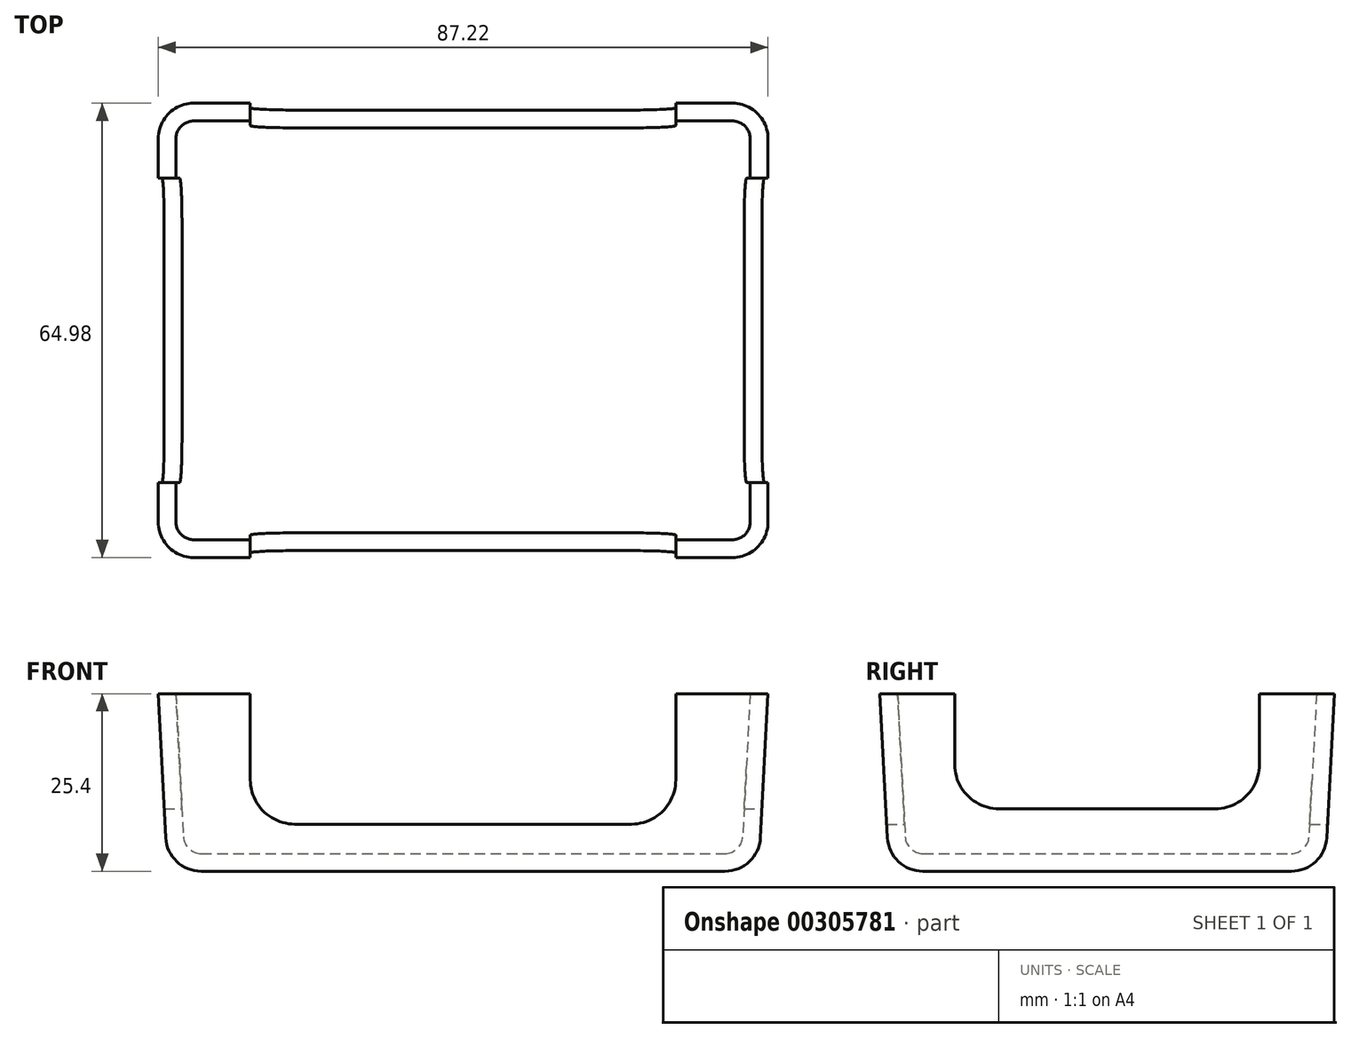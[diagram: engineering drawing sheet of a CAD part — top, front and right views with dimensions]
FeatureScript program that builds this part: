
annotation { "Feature Type Name" : "Feature", "Feature Type Description" : "" }
export const myFeature = defineFeature(function(context is Context, id is Id, definition is map)
    precondition{}
    {
        {
            var Q0;
            Q0=qCreatedBy(makeId("Top.planeOp"),FACE);
            var sketch = newSketch(context, id + "F0", { "sketchPlane" : qUnion([Q0])});
            skLineSegment(sketch, "E0.bottom", {"start": v(42.27, 31.16) * mm, "end": v(-42.27, 31.16) * mm});
            skLineSegment(sketch, "E0.top", {"start": v(42.27, -31.16) * mm, "end": v(-42.27, -31.16) * mm});
            skLineSegment(sketch, "E0.left", {"start": v(42.27, 31.16) * mm, "end": v(42.27, -31.16) * mm});
            skLineSegment(sketch, "E0.right", {"start": v(-42.27, 31.16) * mm, "end": v(-42.27, -31.16) * mm});
            skPoint(sketch, "E0.middle", {"position": v(0, 0) * mm});
            skSolve(sketch);
        }
        {
            var Q0;
            Q0=makeQuery(id+"F0.imprint","IMPRINT",FACE,{"disambiguationData":[TD([[makeQuery(id+"F0.imprint","IMPRINT",EDGE,{"derivedFrom":sQuery(id+"F0.wireOp",EDGE,"E0.bottom")}),1.0]])]});
            extrude(context, id + "F1", {"entities" : qUnion([Q0]), "depth" : 25.4 * mm, "hasDraft" : true, "draftAngle" : 3 * degree});
        }
        {
            var Q0;
            Q0=makeQuery(id+"F1.opExtrude","SWEPT_EDGE",EDGE,{"disambiguationData":[OSD([sQuery(id+"F0.wireOp",EDGE,"E0.top"),sQuery(id+"F0.wireOp",EDGE,"E0.right")])]});
            var Q1;
            Q1=makeQuery(id+"F1.opExtrude","SWEPT_EDGE",EDGE,{"disambiguationData":[OSD([sQuery(id+"F0.wireOp",EDGE,"E0.top"),sQuery(id+"F0.wireOp",EDGE,"E0.left")])]});
            var Q2;
            Q2=makeQuery(id+"F1.opExtrude","CAP_EDGE",EDGE,{"disambiguationData":[OSD([sQuery(id+"F0.wireOp",EDGE,"E0.top")])],"isStart":true});
            var Q3;
            Q3=makeQuery(id+"F1.opExtrude","CAP_EDGE",EDGE,{"disambiguationData":[OSD([sQuery(id+"F0.wireOp",EDGE,"E0.right")])],"isStart":true});
            var Q4;
            Q4=makeQuery(id+"F1.opExtrude","SWEPT_EDGE",EDGE,{"disambiguationData":[OSD([sQuery(id+"F0.wireOp",EDGE,"E0.bottom"),sQuery(id+"F0.wireOp",EDGE,"E0.right")])]});
            var Q5;
            Q5=makeQuery(id+"F1.opExtrude","CAP_EDGE",EDGE,{"disambiguationData":[OSD([sQuery(id+"F0.wireOp",EDGE,"E0.bottom")])],"isStart":true});
            var Q6;
            Q6=makeQuery(id+"F1.opExtrude","CAP_EDGE",EDGE,{"disambiguationData":[OSD([sQuery(id+"F0.wireOp",EDGE,"E0.left")])],"isStart":true});
            var Q7;
            Q7=makeQuery(id+"F1.opExtrude","SWEPT_EDGE",EDGE,{"disambiguationData":[OSD([sQuery(id+"F0.wireOp",EDGE,"E0.bottom"),sQuery(id+"F0.wireOp",EDGE,"E0.left")])]});
            fillet(context, id + "F2", {"entities" : qUnion([Q0, Q1, Q2, Q3, Q4, Q5, Q6, Q7]), "radius" : 5.08 * mm, "tangentPropagation" : true, "allowEdgeOverflow" : false});
        }
        {
            var Q0;
            Q0=qCreatedBy(makeId("Front.planeOp"),FACE);
            var sketch = newSketch(context, id + "F3", { "sketchPlane" : qUnion([Q0])});
            skLineSegment(sketch, "E1.bottom", {"start": v(30.43, 44.07) * mm, "end": v(-30.43, 44.07) * mm});
            skLineSegment(sketch, "E1.top", {"start": v(24.08, 6.73) * mm, "end": v(-24.08, 6.73) * mm});
            skLineSegment(sketch, "E1.left", {"start": v(30.43, 44.07) * mm, "end": v(30.43, 13.08) * mm});
            skLineSegment(sketch, "E1.right", {"start": v(-30.43, 44.07) * mm, "end": v(-30.43, 13.08) * mm});
            skPoint(sketch, "E1.middle", {"position": v(0, 25.4) * mm});
            skPoint(sketch, "E2.visualSharp", {"position": v(-30.43, 6.73) * mm});
            skArc(sketch, "E2.filletArc", {"start": v(-30.43, 13.08) * mm, "mid": v(-28.57, 8.6) * mm, "end": v(-24.08, 6.73) * mm});
            skPoint(sketch, "E3.visualSharp", {"position": v(30.43, 6.73) * mm});
            skArc(sketch, "E3.filletArc", {"start": v(24.08, 6.73) * mm, "mid": v(28.57, 8.6) * mm, "end": v(30.43, 13.08) * mm});
            skSolve(sketch);
        }
        {
            var Q0;
            Q0=makeQuery(id+"F3.imprint","IMPRINT",FACE,{"disambiguationData":[TD([[makeQuery(id+"F3.imprint","IMPRINT",EDGE,{"derivedFrom":sQuery(id+"F3.wireOp",EDGE,"E1.bottom")}),1.0]])]});
            extrude(context, id + "F4", {"entities" : qUnion([Q0]), "operationType" : NewBodyOperationType.REMOVE, "depth" : 81.28 * mm, "symmetric" : true});
        }
        {
            var Q0;
            Q0=qCreatedBy(makeId("Right.planeOp"),FACE);
            var sketch = newSketch(context, id + "F5", { "sketchPlane" : qUnion([Q0])});
            skLineSegment(sketch, "E4.bottom", {"start": v(21.8, 38.98) * mm, "end": v(-21.8, 38.98) * mm});
            skLineSegment(sketch, "E4.top", {"start": v(15.45, 8.93) * mm, "end": v(-15.45, 8.93) * mm});
            skLineSegment(sketch, "E4.left", {"start": v(21.8, 38.98) * mm, "end": v(21.8, 15.28) * mm});
            skLineSegment(sketch, "E4.right", {"start": v(-21.8, 38.98) * mm, "end": v(-21.8, 15.28) * mm});
            skPoint(sketch, "E4.middle", {"position": v(0, 23.96) * mm});
            skPoint(sketch, "E5.visualSharp", {"position": v(-21.8, 8.93) * mm});
            skArc(sketch, "E5.filletArc", {"start": v(-21.8, 15.28) * mm, "mid": v(-19.94, 10.8) * mm, "end": v(-15.45, 8.93) * mm});
            skPoint(sketch, "E6.visualSharp", {"position": v(21.8, 8.93) * mm});
            skArc(sketch, "E6.filletArc", {"start": v(15.45, 8.93) * mm, "mid": v(19.94, 10.8) * mm, "end": v(21.8, 15.28) * mm});
            skSolve(sketch);
        }
        {
            var Q0;
            Q0=makeQuery(id+"F5.imprint","IMPRINT",FACE,{"disambiguationData":[TD([[makeQuery(id+"F5.imprint","IMPRINT",EDGE,{"derivedFrom":sQuery(id+"F5.wireOp",EDGE,"E4.bottom")}),1.0]])]});
            extrude(context, id + "F6", {"entities" : qUnion([Q0]), "operationType" : NewBodyOperationType.REMOVE, "oppositeDirection" : true, "depth" : 98.04 * mm, "hasSecondDirection" : true, "secondDirectionOppositeDirection" : false, "secondDirectionDepth" : 25.4 * mm, "symmetric" : true});
        }
        {
            var Q0;
            {var subQ0=sQuery(id+"F0.wireOp",EDGE,"E0.bottom");var subQ1=sQuery(id+"F0.wireOp",EDGE,"E0.right");var subQ2=sQuery(id+"F0.wireOp",EDGE,"E0.top");Q0=makeQuery(id+"F4.boolean.opBoolean","SPLIT",FACE,{"disambiguationData":[TD([makeQuery(id+"F1.opExtrude","SWEPT_FACE",FACE,{"disambiguationData":[OSD([subQ1])]})])],"derivedFrom":makeQuery(id+"F1.opExtrude","CAP_FACE",FACE,{"disambiguationData":[OSD([subQ0,subQ2,sQuery(id+"F0.wireOp",EDGE,"E0.left"),subQ1])],"isStart":false})});}
            var Q1;
            Q1=makeQuery(id+"F4.boolean.opBoolean","COPY",FACE,{"derivedFrom":makeQuery(id+"F4.opExtrude","SWEPT_FACE",FACE,{"disambiguationData":[OSD([sQuery(id+"F3.wireOp",EDGE,"E1.right")])]})});
            var Q2;
            Q2=makeQuery(id+"F4.boolean.opBoolean","COPY",FACE,{"derivedFrom":makeQuery(id+"F4.opExtrude","SWEPT_FACE",FACE,{"disambiguationData":[OSD([sQuery(id+"F3.wireOp",EDGE,"E1.top")])]})});
            var Q3;
            Q3=makeQuery(id+"F4.boolean.opBoolean","COPY",FACE,{"derivedFrom":makeQuery(id+"F4.opExtrude","SWEPT_FACE",FACE,{"disambiguationData":[OSD([sQuery(id+"F3.wireOp",EDGE,"E1.left")])]})});
            var Q4;
            {var subQ0=sQuery(id+"F0.wireOp",EDGE,"E0.bottom");var subQ1=sQuery(id+"F0.wireOp",EDGE,"E0.top");var subQ2=sQuery(id+"F0.wireOp",EDGE,"E0.left");Q4=makeQuery(id+"F4.boolean.opBoolean","SPLIT",FACE,{"disambiguationData":[TD([makeQuery(id+"F1.opExtrude","SWEPT_FACE",FACE,{"disambiguationData":[OSD([subQ2])]})])],"derivedFrom":makeQuery(id+"F1.opExtrude","CAP_FACE",FACE,{"disambiguationData":[OSD([subQ0,subQ1,subQ2,sQuery(id+"F0.wireOp",EDGE,"E0.right")])],"isStart":false})});}
            var Q5;
            Q5=makeQuery(id+"F4.boolean.opBoolean","COPY",FACE,{"derivedFrom":makeQuery(id+"F4.opExtrude","SWEPT_FACE",FACE,{"disambiguationData":[OSD([sQuery(id+"F3.wireOp",EDGE,"E3.filletArc")])]})});
            var Q6;
            Q6=makeQuery(id+"F4.boolean.opBoolean","COPY",FACE,{"derivedFrom":makeQuery(id+"F4.opExtrude","SWEPT_FACE",FACE,{"disambiguationData":[OSD([sQuery(id+"F3.wireOp",EDGE,"E2.filletArc")])]})});
            var Q7;
            {var subQ0=sQuery(id+"F0.wireOp",EDGE,"E0.right");Q7=makeQuery(id+"F6.boolean.opBoolean","COPY",FACE,{"disambiguationData":[TD([makeQuery(id+"F1.opExtrude","SWEPT_FACE",FACE,{"disambiguationData":[OSD([subQ0])]})])],"derivedFrom":makeQuery(id+"F6.opExtrude","SWEPT_FACE",FACE,{"disambiguationData":[OSD([sQuery(id+"F5.wireOp",EDGE,"E4.left")])]})});}
            var Q8;
            Q8=makeQuery(id+"F6.boolean.opBoolean","COPY",FACE,{"disambiguationData":[TD([makeQuery(id+"F1.opExtrude","SWEPT_FACE",FACE,{"disambiguationData":[OSD([sQuery(id+"F0.wireOp",EDGE,"E0.right")])]})])],"derivedFrom":makeQuery(id+"F6.opExtrude","SWEPT_FACE",FACE,{"disambiguationData":[OSD([sQuery(id+"F5.wireOp",EDGE,"E6.filletArc")])]})});
            var Q9;
            Q9=makeQuery(id+"F6.boolean.opBoolean","COPY",FACE,{"disambiguationData":[TD([makeQuery(id+"F1.opExtrude","SWEPT_FACE",FACE,{"disambiguationData":[OSD([sQuery(id+"F0.wireOp",EDGE,"E0.right")])]})])],"derivedFrom":makeQuery(id+"F6.opExtrude","SWEPT_FACE",FACE,{"disambiguationData":[OSD([sQuery(id+"F5.wireOp",EDGE,"E4.top")])]})});
            var Q10;
            Q10=makeQuery(id+"F6.boolean.opBoolean","COPY",FACE,{"disambiguationData":[TD([makeQuery(id+"F1.opExtrude","SWEPT_FACE",FACE,{"disambiguationData":[OSD([sQuery(id+"F0.wireOp",EDGE,"E0.right")])]})])],"derivedFrom":makeQuery(id+"F6.opExtrude","SWEPT_FACE",FACE,{"disambiguationData":[OSD([sQuery(id+"F5.wireOp",EDGE,"E5.filletArc")])]})});
            var Q11;
            Q11=makeQuery(id+"F6.boolean.opBoolean","COPY",FACE,{"disambiguationData":[TD([makeQuery(id+"F1.opExtrude","SWEPT_FACE",FACE,{"disambiguationData":[OSD([sQuery(id+"F0.wireOp",EDGE,"E0.left")])]})])],"derivedFrom":makeQuery(id+"F6.opExtrude","SWEPT_FACE",FACE,{"disambiguationData":[OSD([sQuery(id+"F5.wireOp",EDGE,"E6.filletArc")])]})});
            var Q12;
            {var subQ0=sQuery(id+"F0.wireOp",EDGE,"E0.left");Q12=makeQuery(id+"F6.boolean.opBoolean","COPY",FACE,{"disambiguationData":[TD([makeQuery(id+"F1.opExtrude","SWEPT_FACE",FACE,{"disambiguationData":[OSD([subQ0])]})])],"derivedFrom":makeQuery(id+"F6.opExtrude","SWEPT_FACE",FACE,{"disambiguationData":[OSD([sQuery(id+"F5.wireOp",EDGE,"E4.left")])]})});}
            var Q13;
            Q13=makeQuery(id+"F6.boolean.opBoolean","COPY",FACE,{"disambiguationData":[TD([makeQuery(id+"F1.opExtrude","SWEPT_FACE",FACE,{"disambiguationData":[OSD([sQuery(id+"F0.wireOp",EDGE,"E0.left")])]})])],"derivedFrom":makeQuery(id+"F6.opExtrude","SWEPT_FACE",FACE,{"disambiguationData":[OSD([sQuery(id+"F5.wireOp",EDGE,"E4.top")])]})});
            var Q14;
            Q14=makeQuery(id+"F6.boolean.opBoolean","COPY",FACE,{"disambiguationData":[TD([makeQuery(id+"F1.opExtrude","SWEPT_FACE",FACE,{"disambiguationData":[OSD([sQuery(id+"F0.wireOp",EDGE,"E0.left")])]})])],"derivedFrom":makeQuery(id+"F6.opExtrude","SWEPT_FACE",FACE,{"disambiguationData":[OSD([sQuery(id+"F5.wireOp",EDGE,"E5.filletArc")])]})});
            var Q15;
            {var subQ0=sQuery(id+"F0.wireOp",EDGE,"E0.left");Q15=makeQuery(id+"F6.boolean.opBoolean","COPY",FACE,{"disambiguationData":[TD([makeQuery(id+"F1.opExtrude","SWEPT_FACE",FACE,{"disambiguationData":[OSD([subQ0])]})])],"derivedFrom":makeQuery(id+"F6.opExtrude","SWEPT_FACE",FACE,{"disambiguationData":[OSD([sQuery(id+"F5.wireOp",EDGE,"E4.right")])]})});}
            var Q16;
            {var subQ0=sQuery(id+"F0.wireOp",EDGE,"E0.right");Q16=makeQuery(id+"F6.boolean.opBoolean","COPY",FACE,{"disambiguationData":[TD([makeQuery(id+"F1.opExtrude","SWEPT_FACE",FACE,{"disambiguationData":[OSD([subQ0])]})])],"derivedFrom":makeQuery(id+"F6.opExtrude","SWEPT_FACE",FACE,{"disambiguationData":[OSD([sQuery(id+"F5.wireOp",EDGE,"E4.right")])]})});}
            shell(context, id + "F7", {"entities" : qUnion([Q0, Q1, Q2, Q3, Q4, Q5, Q6, Q7, Q8, Q9, Q10, Q11, Q12, Q13, Q14, Q15, Q16]), "thickness" : 2.54 * mm});
        }
    });
